# Revit family: P500330-031
name_source: partatom
category: Lighting Fixtures
units: mm (PartAtom-declared; Revit-internal decimal feet)

## family parameters
Cut with Voids When Loaded = No
Host = Face
Light Source = No
OmniClass Number = 23.80.70.11.14.17
OmniClass Title = Direct/Indirect
Part Type = Normal
Room Calculation Point = No
Round Connector Dimension = Use Diameter
Shared = Yes

## types (1)
- P500330-031
    Apparent Load = 60 VA
    Assembly Code = D5020200
    Connector Description = Lighting Connector
    Default Elevation = 48 "
    Description = Lowery Collection Five-Light Textured Black/Distressed Gold Hanging Pendant Light
    Features = Application: Raise the bar on contemporary design with the Lowery Collection 5-Light Black/Distressed Gold Modern Hanging Pendant Light is ideal for any foyer, dining room, kitchen, breakfast nook, entryway, living room, or sitting room.
Styles: Perfect for contemporary and modern style settings.
Finish: Layered rectangular shields coated in a textured black iron finish are artistically combined with distressed gold leaf panels against a black frame.
Materials: Constructed from steel to ensure a long product lifespan.
Glass/Shades: Light sources glowing from inside the structure cast a shimmering reflective light that highlights the beautiful contrast between light and dark.
Bulbs: For ideal illumination, use 5 medium base bulbs that are sold separately (60w max - LED/CFL/incandescent). Compatible with dimmable bulbs.
Dimensions: Measures 26-inch diameter by 20-inch height.
Certifications: cULus dry location listed.
Pairs With: Pairs with the Adagio, Orrizo, and Rae collections from Progress Lighting.
Warranty: Our 1-Year Limited Warranty guarantees your complete satisfaction with your purchase and includes professional after-sales customer service support.
    Fixture distribution = Direct
    Glass = Paint - Hubbell - White Texture
    Gold = Hubbell - Gold
    Height = 20 "
    Housing Material = Paint - Hubbell - Textured Camera Black
    Lamp = LED/CFL/incandescent
    Length = 26 "
    Load Classification = Lighting
    Manufacturer = Progress Lighting
    Model = P500330-031
    Power Factor = 1
    Product Documentation Link = https://hubbellcdn.com
    Product Link = https://www.hubbell.com
    URL = https://www.hubbell.com
    Voltage = 120 V
    Warranty = 1 year Warranty
    Wattage Comments = 60W
    Watts = 60 W
    Wood = Hubbell - Oak

## geometry (parser evidence)
native form markers: Sweep x4
no freeform markers — native parametric forms only
